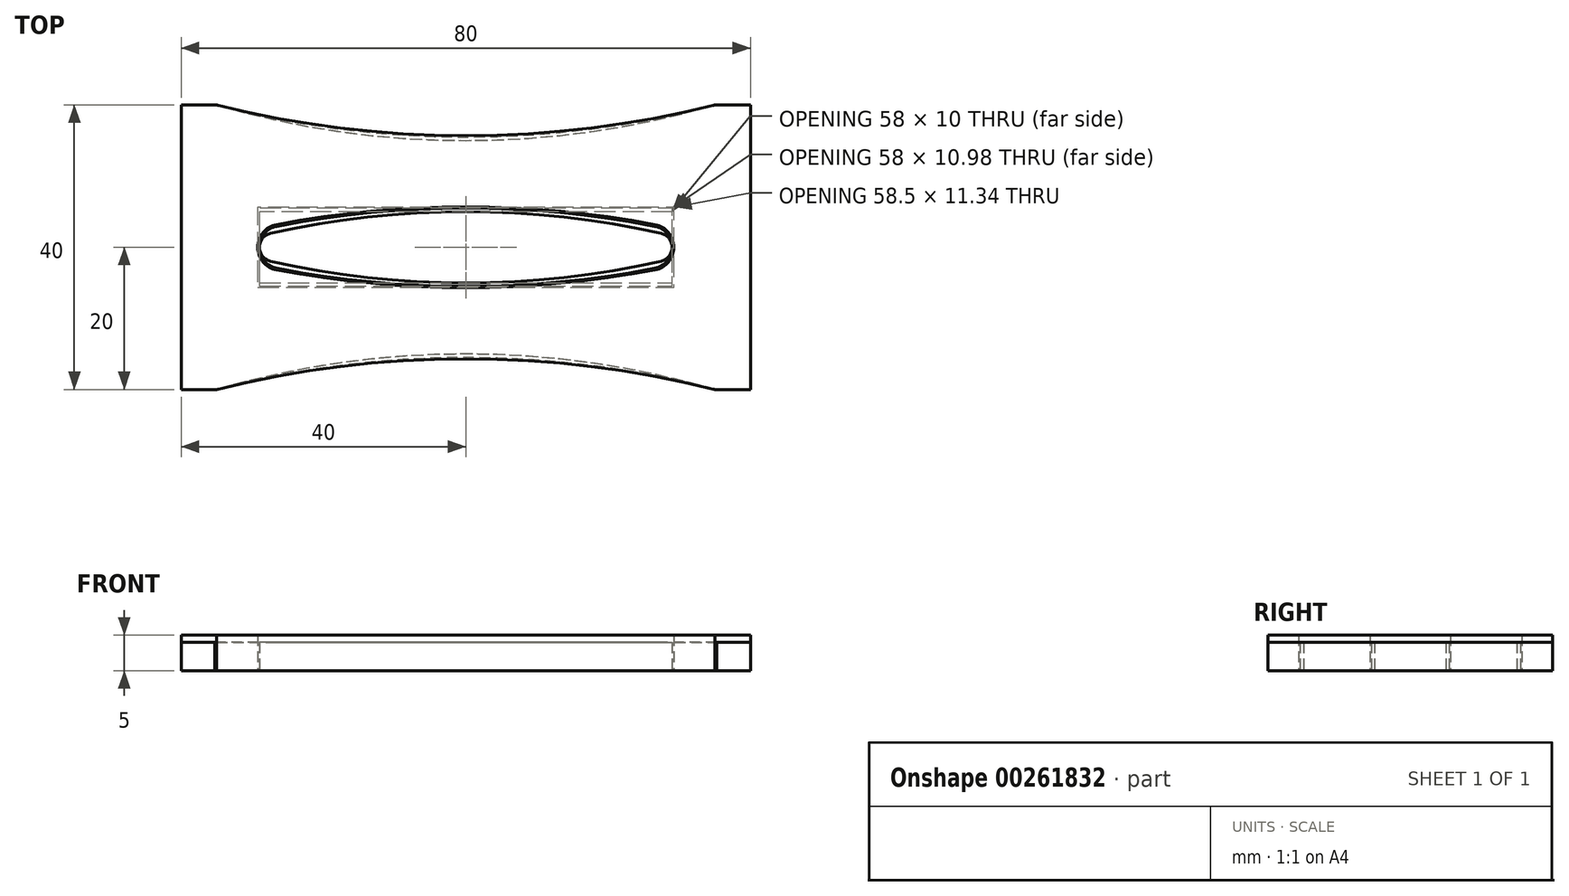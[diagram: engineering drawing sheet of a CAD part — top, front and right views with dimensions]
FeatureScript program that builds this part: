
annotation { "Feature Type Name" : "Feature", "Feature Type Description" : "" }
export const myFeature = defineFeature(function(context is Context, id is Id, definition is map)
    precondition{}
    {
        {
            var Q0;
            Q0=qCreatedBy(makeId("Top.planeOp"),FACE);
            var sketch = newSketch(context, id + "F0", { "sketchPlane" : qUnion([Q0])});
            skLineSegment(sketch, "E0.bottom", {"start": v(40, -20) * mm, "end": v(35.25, -20) * mm});
            skLineSegment(sketch, "E0.top", {"start": v(40, 20) * mm, "end": v(35.25, 20) * mm});
            skLineSegment(sketch, "E0.left", {"start": v(40, -20) * mm, "end": v(40, 20) * mm});
            skLineSegment(sketch, "E0.right", {"start": v(-40, -20) * mm, "end": v(-40, 20) * mm});
            skLineSegment(sketch, "E1", {"start": v(-40, 0) * mm, "end": v(0, 0) * mm});
            skLineSegment(sketch, "E2", {"start": v(0, 0) * mm, "end": v(0, 20) * mm});
            skCircle(sketch, "E3", {"center": v(-26, 0) * mm, "radius": 3 * mm});
            skCircle(sketch, "E4.MirrorC", {"center": v(26, 0) * mm, "radius": 3 * mm});
            skArc(sketch, "E5", {"start": v(26.57, 2.95) * mm, "mid": v(0, 5.49) * mm, "end": v(-26.57, 2.95) * mm});
            skArc(sketch, "E6.MirrorCS", {"start": v(26.57, -2.95) * mm, "mid": v(0, -5.49) * mm, "end": v(-26.57, -2.95) * mm});
            skArc(sketch, "E7", {"start": v(-35.25, 20) * mm, "mid": v(0, 15.49) * mm, "end": v(35.25, 20) * mm});
            skLineSegment(sketch, "E8.trimOffspring", {"start": v(-35.25, 20) * mm, "end": v(-40, 20) * mm});
            skArc(sketch, "E9.MirrorCS", {"start": v(-35.25, -20) * mm, "mid": v(0, -15.49) * mm, "end": v(35.25, -20) * mm});
            skLineSegment(sketch, "E10.trimOffspring", {"start": v(-35.25, -20) * mm, "end": v(-40, -20) * mm});
            skSolve(sketch);
        }
        {
            var Q0;
            Q0=qCreatedBy(makeId("Top.planeOp"),FACE);
            var sketch = newSketch(context, id + "F1", { "sketchPlane" : qUnion([Q0])});
            skLineSegment(sketch, "E11.bottom", {"start": v(40, -20) * mm, "end": v(35.04, -20) * mm});
            skLineSegment(sketch, "E11.top", {"start": v(40, 20) * mm, "end": v(35.04, 20) * mm});
            skLineSegment(sketch, "E11.left", {"start": v(40, -20) * mm, "end": v(40, 20) * mm});
            skLineSegment(sketch, "E11.right", {"start": v(-40, -20) * mm, "end": v(-40, 20) * mm});
            skLineSegment(sketch, "E12", {"start": v(-40, 0) * mm, "end": v(-29.25, 0) * mm});
            skLineSegment(sketch, "E13", {"start": v(0, 0) * mm, "end": v(0, 20) * mm});
            skArc(sketch, "E14", {"start": v(-26.6, 3.2) * mm, "mid": v(-29.25, 0) * mm, "end": v(-26.6, -3.2) * mm});
            skArc(sketch, "E15.MirrorC", {"start": v(26.6, 3.2) * mm, "mid": v(29.25, 0) * mm, "end": v(26.6, -3.2) * mm});
            skArc(sketch, "E16", {"start": v(26.6, 3.2) * mm, "mid": v(0, 5.67) * mm, "end": v(-26.6, 3.2) * mm});
            skArc(sketch, "E17.MirrorCS", {"start": v(26.6, -3.2) * mm, "mid": v(0, -5.67) * mm, "end": v(-26.6, -3.2) * mm});
            skArc(sketch, "E18", {"start": v(-35.04, 20) * mm, "mid": v(0, 15.67) * mm, "end": v(35.04, 20) * mm});
            skLineSegment(sketch, "E19.trimOffspring", {"start": v(-35.04, 20) * mm, "end": v(-40, 20) * mm});
            skArc(sketch, "E20.MirrorCS", {"start": v(-35.04, -20) * mm, "mid": v(0, -15.67) * mm, "end": v(35.04, -20) * mm});
            skLineSegment(sketch, "E21.trimOffspring", {"start": v(-35.04, -20) * mm, "end": v(-40, -20) * mm});
            skLineSegment(sketch, "E22.trimOffspring", {"start": v(-26, 0) * mm, "end": v(0, 0) * mm});
            skSolve(sketch);
        }
        {
            var Q0;
            {var subQ11=sQuery(id+"F0.wireOp",EDGE,"E8.trimOffspring");Q0=makeQuery(id+"F0.imprint","IMPRINT",FACE,{"disambiguationData":[TD([[makeQuery(id+"F0.imprint","IMPRINT",EDGE,{"derivedFrom":subQ11}),1.0]])]});}
            var Q1;
            Q1=makeQuery(id+"F0.imprint","IMPRINT",FACE,{"disambiguationData":[TD([[makeQuery(id+"F0.imprint","IMPRINT",EDGE,{"derivedFrom":sQuery(id+"F0.wireOp",EDGE,"E0.bottom")}),-1.0]])]});
            extrude(context, id + "F2", {"entities" : qUnion([Q0, Q1]), "depth" : 4 * mm});
        }
        {
            var Q0;
            Q0=makeQuery(id+"F1.imprint","IMPRINT",FACE,{"disambiguationData":[TD([[makeQuery(id+"F1.imprint","IMPRINT",EDGE,{"derivedFrom":sQuery(id+"F1.wireOp",EDGE,"E11.bottom")}),-1.0]])]});
            var Q1;
            {var subQ1=sQuery(id+"F1.wireOp",EDGE,"E12");Q1=makeQuery(id+"F1.imprint","IMPRINT",FACE,{"disambiguationData":[TD([[makeQuery(id+"F1.imprint","IMPRINT",EDGE,{"derivedFrom":subQ1}),1.0]])]});}
            extrude(context, id + "F3", {"entities" : qUnion([Q0, Q1]), "depth" : 5 * mm});
        }
        {
            var Q0;
            Q0=qCreatedBy(makeId("Top.planeOp"),FACE);
            var sketch = newSketch(context, id + "F4", { "sketchPlane" : qUnion([Q0])});
            skLineSegment(sketch, "E23.bottom", {"start": v(40, -20) * mm, "end": v(35, -20) * mm});
            skLineSegment(sketch, "E23.top", {"start": v(40, 20) * mm, "end": v(35, 20) * mm});
            skLineSegment(sketch, "E23.left", {"start": v(40, -20) * mm, "end": v(40, 20) * mm});
            skLineSegment(sketch, "E23.right", {"start": v(-40, -20) * mm, "end": v(-40, 20) * mm});
            skLineSegment(sketch, "E24", {"start": v(-40, 0) * mm, "end": v(0, 0) * mm});
            skLineSegment(sketch, "E25", {"start": v(0, 0) * mm, "end": v(0, 20) * mm});
            skCircle(sketch, "E26", {"center": v(-27, 0) * mm, "radius": 2 * mm});
            skCircle(sketch, "E27.MirrorC", {"center": v(27, 0) * mm, "radius": 2 * mm});
            skArc(sketch, "E28", {"start": v(27.44, 1.95) * mm, "mid": v(0, 5) * mm, "end": v(-27.44, 1.95) * mm});
            skArc(sketch, "E29.MirrorCS", {"start": v(27.44, -1.95) * mm, "mid": v(0, -5) * mm, "end": v(-27.44, -1.95) * mm});
            skArc(sketch, "E30", {"start": v(-35, 20) * mm, "mid": v(0, 15) * mm, "end": v(35, 20) * mm});
            skLineSegment(sketch, "E31.trimOffspring", {"start": v(-35, 20) * mm, "end": v(-40, 20) * mm});
            skArc(sketch, "E32.MirrorCS", {"start": v(-35, -20) * mm, "mid": v(0, -15) * mm, "end": v(35, -20) * mm});
            skLineSegment(sketch, "E33.trimOffspring", {"start": v(-35, -20) * mm, "end": v(-40, -20) * mm});
            skSolve(sketch);
        }
        {
            var Q0;
            Q0=makeQuery(id+"F4.imprint","IMPRINT",FACE,{"disambiguationData":[TD([[makeQuery(id+"F4.imprint","IMPRINT",EDGE,{"derivedFrom":sQuery(id+"F4.wireOp",EDGE,"E23.bottom")}),-1.0]])]});
            var Q1;
            {var subQ11=sQuery(id+"F4.wireOp",EDGE,"E31.trimOffspring");Q1=makeQuery(id+"F4.imprint","IMPRINT",FACE,{"disambiguationData":[TD([[makeQuery(id+"F4.imprint","IMPRINT",EDGE,{"derivedFrom":subQ11}),1.0]])]});}
            extrude(context, id + "F5", {"entities" : qUnion([Q0, Q1]), "depth" : 4 * mm});
        }
    });
